# Revit family: HC_Storage Tank_MEPcontent_De Dietrich Thermique_DHW_BLC
name_source: partatom
category: Mechanical Equipment
revit_build: Autodesk Revit 2018 (Build: 20170223_1515(x64)
units: mm (PartAtom-declared; Revit-internal decimal feet)

## family parameters
Always vertical = Yes
Cut with Voids When Loaded = No
OmniClass Number = 23.75.10.34.11
OmniClass Title = Energy Storage Tanks
Part Type = Normal
Room Calculation Point = No
Round Connector Dimension = Use Diameter
Shared = No
Work Plane-Based = No

## types (5) — shared parameters
Article Description = “Comfort”, independent calorifiers
Black = Color RGB 020-020-020
Boiler Top = 40 mm
Content Supplier URL = www.MEPcontent.com
Custom = No
Description = “Comfort”, independent calorifiers
Domestic Cold Water Diameter = 25 mm  [stored 0.082021 ft]
Domestic Hot Water Diameter 1 = 25 mm  [stored 0.082021 ft]
Domestic Hot Water Diameter 2 = 19 mm  [stored 0.062336 ft]
Domestic Hot Water Maximum Flow (at ΔT=30K – EN13203-1) = 0.0 L/s
EMCS Version = 2.0
ETIM Article Class = EC010184
Family Version = 11.14
Grey = Color RAL 9006
Hydronic Return Diameter = 25 mm  [stored 0.082021 ft]
Hydronic Supply Diameter = 25 mm  [stored 0.082021 ft]
IFCExportAs = IfcTankType
IFCExportType = NOTDEFINED
MEPcontent Class = STORAGE_TANK_HC
Manufacturer = De Dietrich Thermique
Manufacturer URL = http://www.dedietrich-thermique.fr
Product Line = De Dietrich Thermique
Revit Version = 2018
Service Area = Color RGB 218-227-224
URL = www.stabiplan.com
Use Nominal Diameter = Yes
White = Color RAL 9016
zero-valued in all types: Offset

## per-type parameters (varying)
| type | A | B | C | Cap Visibility | Cap Void | Connection Length | D | E | F | Feet Position | G | GTIN | Logo Void | Manufacturer Art. No. | Radius | Service Area Offset | Volume |
| BLC 150 | 70 mm  [stored 0.229659 ft] | 282 mm | 567 mm  [stored 1.86024 ft] | No | 306 mm | 326 mm | 662 mm  [stored 2.17192 ft] | 844 mm  [stored 2.76903 ft] | 605 mm  [stored 1.98491 ft] | 218 mm | 944 mm | 3661238547919 | 305 mm | 100018088 | 303 mm | 349 mm | 150.0 L |
| BLC 200 | 70 mm  [stored 0.229659 ft] | 282 mm | 657 mm | Yes | 306 mm | 326 mm | 840 mm | 1114 mm | 605 mm  [stored 1.98491 ft] | 218 mm | 1212 mm | 3661238547926 | 305 mm | 100018089 | 303 mm | 375 mm | 200.0 L |
| BLC 300 | 70 mm  [stored 0.229659 ft] | 282 mm | 747 mm | Yes | 306 mm | 326 mm | 1142 mm | 1634 mm | 605 mm  [stored 1.98491 ft] | 218 mm | 1734 mm | 3661238547933 | 305 mm | 100018090 | 303 mm | 375 mm | 300.0 L |
| BLC 400 | 66 mm | 284 mm | 838 mm | Yes | 356 mm | 376 mm | 1157 mm | 1510 mm | 705 mm | 268 mm | 1622 mm | 3661238547940 | 355 mm | 100018091 | 353 mm | 375 mm | 395.0 L |
| BLC 500 | 71 mm | 283 mm | 896 mm | Yes | 381 mm  [stored 1.25 ft] | 401 mm | 1213 mm | 1618 mm | 755 mm | 293 mm | 1740 mm | 3661238547957 | 380 mm | 100018092 | 378 mm | 375 mm | 500.0 L |

note: column(s) folded — value = type name in every type: Article Type, Model

note: [stored X ft] marks values corroborated as IEEE doubles in the binary element streams (Revit-internal decimal feet)

## geometry (parser evidence)
native form markers: Sweep x2
no freeform markers — native parametric forms only
